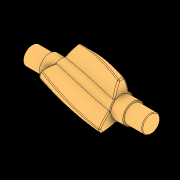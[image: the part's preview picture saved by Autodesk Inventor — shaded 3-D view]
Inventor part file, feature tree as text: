
AUTODESK INVENTOR PART (.ipt)
format: ipt  version: 2020 (Build 240168000, 168)  size: 702,976 bytes
history: native  units: mm
features: other x4, extrude x1, chamfer x1, sketch x1
ambient origin geometry x8: Origin, YZ Plane, XZ Plane, XY Plane, X Axis, Y Axis, Z Axis, Center Point
bodies: Body1 (feature_tree)
feature tree (7):
  other  "WormA.ipt"
  extrude  "擠出1"  Depth=110.0mm
  chamfer  "倒角1"  Distance=33.0mm
  other  "實體1::WormA.ipt"
  other  "標籤特徵1"
  sketch  "草圖1"
  other  "實體1"
